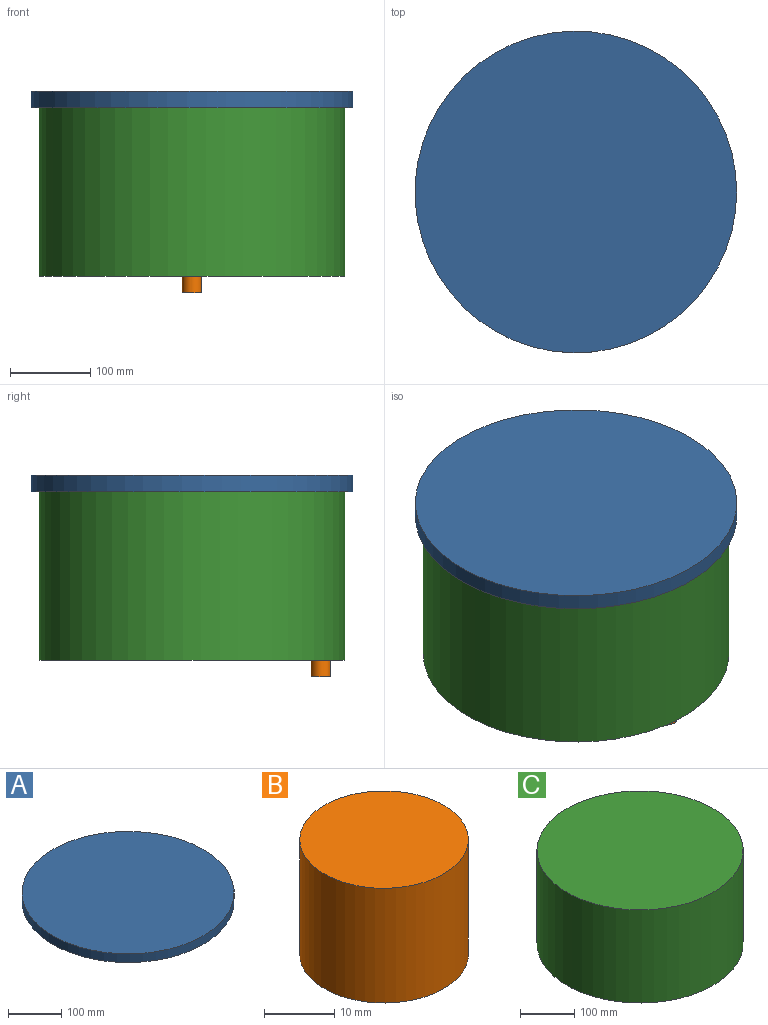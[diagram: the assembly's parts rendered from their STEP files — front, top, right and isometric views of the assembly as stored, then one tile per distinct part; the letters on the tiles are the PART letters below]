
ASSEMBLY  parts=3 mates=1
PART A: 3 faces, bbox 400x400x20 mm
  f0: cylinder r=200mm len=400mm, axis (0,0,1), area 25132.7mm2, adj f1,f2
  f1: plane 400x400mm, normal (0,0,1), area 125663.7mm2, adj f0
  f2: plane 400x400mm, normal (0,0,-1), area 125663.7mm2, adj f0
PART B: 5 faces, bbox 24x24x20 mm
  f0: cylinder r=12mm len=24mm, axis (0,0,1), area 1508mm2, adj f1,f2
  f1: plane 24x24mm, normal (0,0,1), area 452.4mm2, adj f0
  f2: plane 24x24mm, normal (0,0,-1), area 426mm2, adj f0,f3
  f3: cylinder r=2.9mm len=5.8mm, axis (0,0,-1), area 91.1mm2, adj f2,f4
  f4: plane 5.8x5.8mm, normal (0,0,-1), area 26.4mm2, adj f3
PART C: 3 faces, bbox 380x380x210 mm
  f0: cylinder r=190mm len=380mm, axis (0,0,1), area 250699.1mm2, adj f1,f2
  f1: plane 380x380mm, normal (0,0,1), area 113411.5mm2, adj f0
  f2: plane 380x380mm, normal (0,0,-1), area 113411.5mm2, adj f0
PLACE A t=(-49.36,-14.19,11.46)mm
PLACE B rot(axis=(1,0,0),180deg) t=(-49.36,-174.19,-198.54)mm
PLACE C rot(axis=(1,0,0),180deg) t=(-49.36,-14.19,11.46)mm
MATE fastened C.f0 <-> A.f0  axis (0,0,1) through (-49.36,-14.19,11.46)mm
